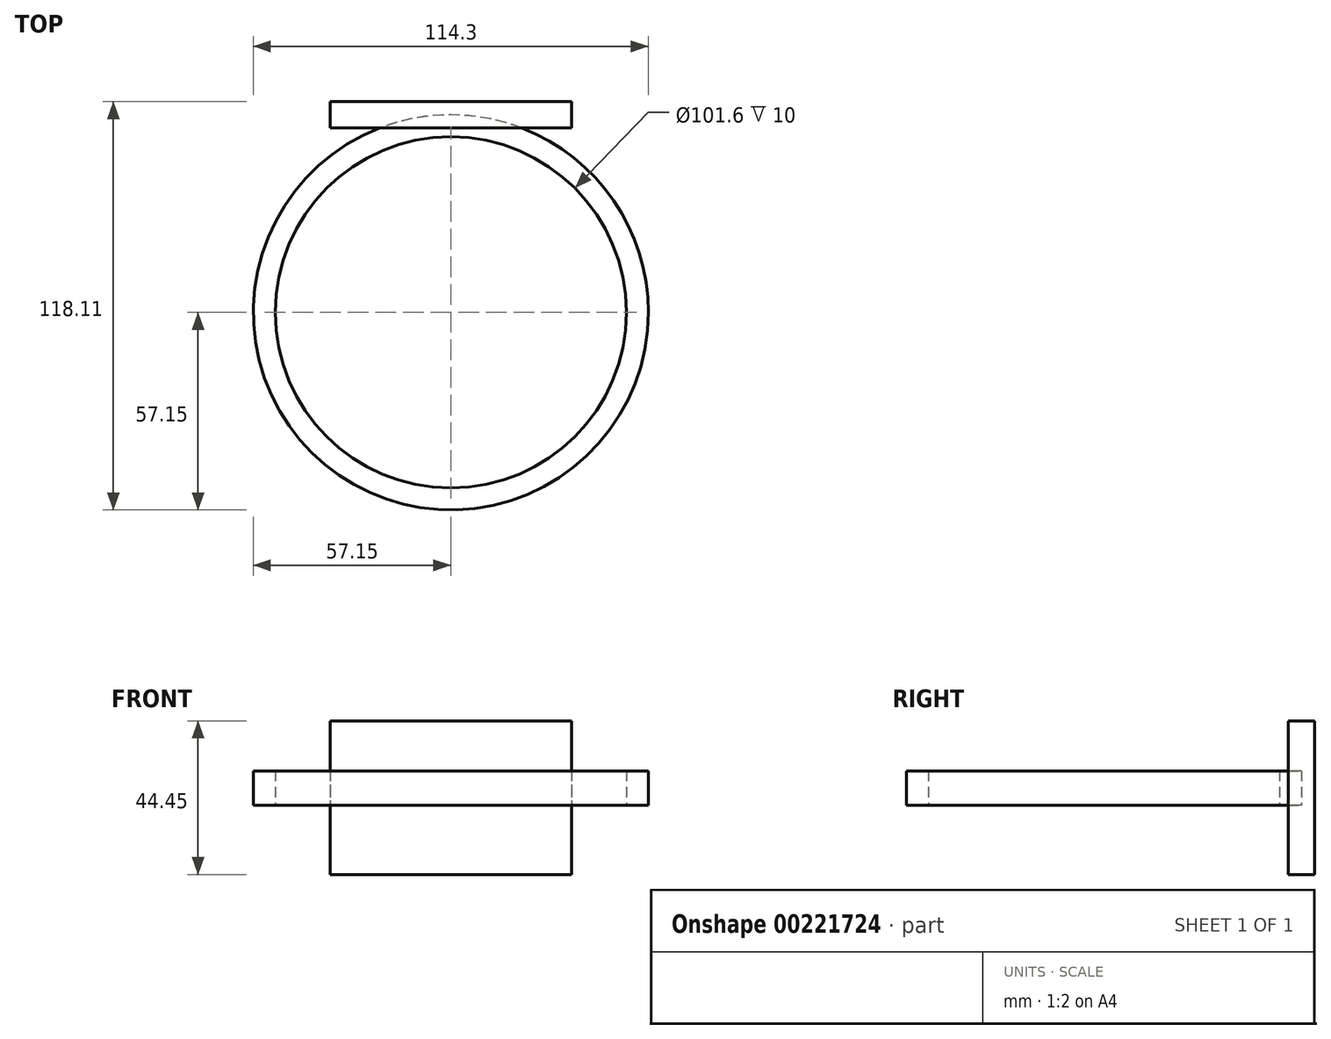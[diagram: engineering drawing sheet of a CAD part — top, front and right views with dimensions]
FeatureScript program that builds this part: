
annotation { "Feature Type Name" : "Feature", "Feature Type Description" : "" }
export const myFeature = defineFeature(function(context is Context, id is Id, definition is map)
    precondition{}
    {
        {
            var Q0;
            Q0=qCreatedBy(makeId("Front.planeOp"),FACE);
            var sketch = newSketch(context, id + "F0", { "sketchPlane" : qUnion([Q0])});
            skLineSegment(sketch, "E0.bottom", {"start": v(-34.92, -8.33) * mm, "end": v(34.93, -8.33) * mm});
            skLineSegment(sketch, "E0.top", {"start": v(-34.93, -52.78) * mm, "end": v(34.93, -52.78) * mm});
            skLineSegment(sketch, "E0.left", {"start": v(-34.92, -8.33) * mm, "end": v(-34.92, -52.78) * mm});
            skLineSegment(sketch, "E0.right", {"start": v(34.93, -8.33) * mm, "end": v(34.93, -52.78) * mm});
            skPoint(sketch, "E0.middle", {"position": v(0, -30.56) * mm});
            skPoint(sketch, "E1.centerSnap0", {"position": v(0, -52.78) * mm});
            skSolve(sketch);
        }
        {
            var Q0;
            Q0=qCreatedBy(makeId("Right.planeOp"),FACE);
            var sketch = newSketch(context, id + "F1", { "sketchPlane" : qUnion([Q0])});
            skLineSegment(sketch, "E2", {"start": v(0, -32.82) * mm, "end": v(-57.15, -32.82) * mm});
            skCircle(sketch, "E3", {"center": v(-57.15, -32.82) * mm, "radius": 57.15 * mm});
            skSolve(sketch);
        }
        {
            var Q0;
            Q0=makeQuery(id+"F1.imprint","IMPRINT",FACE,{"disambiguationData":[TD([[makeQuery(id+"F1.imprint","IMPRINT",EDGE,{"derivedFrom":sQuery(id+"F1.wireOp",EDGE,"E3")}),1.0]])]});
            extrude(context, id + "F2", {"entities" : qUnion([Q0]), "depth" : 10 * mm});
        }
        {
            var Q0;
            Q0=makeQuery(id+"F0.imprint","IMPRINT",FACE,{"disambiguationData":[TD([[makeQuery(id+"F0.imprint","IMPRINT",EDGE,{"derivedFrom":sQuery(id+"F0.wireOp",EDGE,"E0.bottom")}),-1.0]])]});
            extrude(context, id + "F3", {"entities" : qUnion([Q0]), "endBound" : BoundingType.SYMMETRIC, "depth" : 7.62 * mm});
        }
        {
            var Q0;
            Q0=sQuery(id+"F1.wireOp",VERTEX,"E3.center");
            var Q1;
            Q1=makeQuery(id+"F2.opExtrude","SWEPT_BODY",BODY,{"disambiguationData":[OSD([sQuery(id+"F1.wireOp",EDGE,"E3")])]});
            hole(context, id + "F4", {"style" : HoleStyle.SIMPLE, "endStyle" : HoleEndStyle.THROUGH, "oppositeDirection" : true, "holeDiameter" : 101.6 * mm, "locations" : qUnion([Q0]), "scope" : qUnion([Q1]), "isTappedThrough" : true});
        }
        {
            var Q0;
            Q0=makeQuery(id+"F2.opExtrude","SWEPT_BODY",BODY,{"disambiguationData":[OSD([sQuery(id+"F1.wireOp",EDGE,"E3")])]});
            var Q1;
            Q1=sQuery(id+"F1.wireOp",EDGE,"E2");
            transform(context, id + "F5", {"entities" : qUnion([Q0]), "transformType" : TransformType.ROTATION, "transformAxis" : qUnion([Q1]), "angle" : 90 * degree, "makeCopy" : false});
        }
    });
